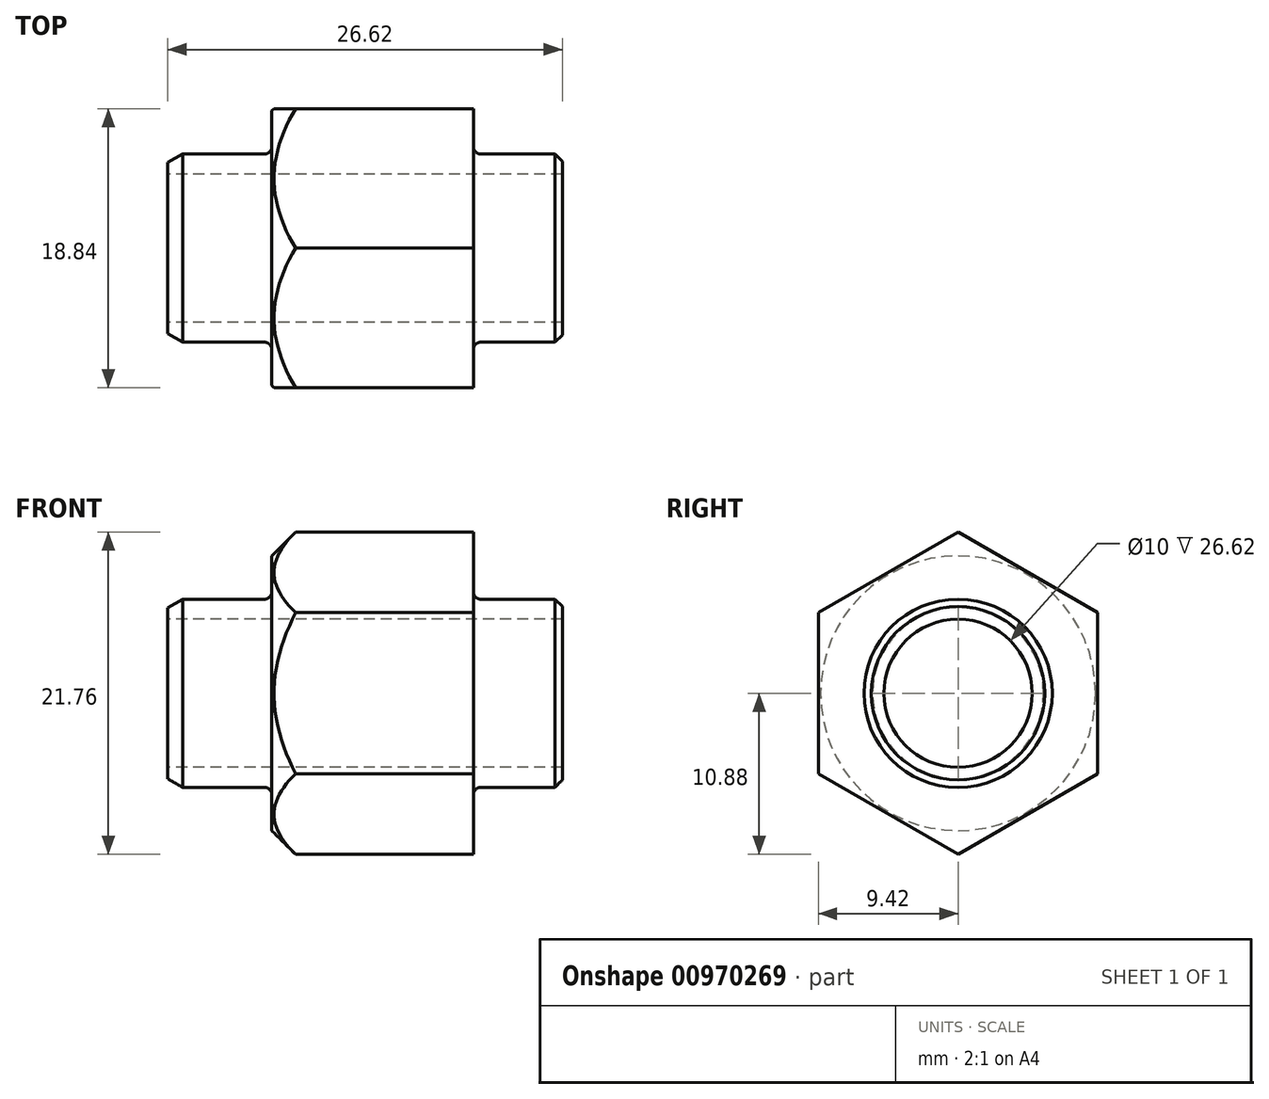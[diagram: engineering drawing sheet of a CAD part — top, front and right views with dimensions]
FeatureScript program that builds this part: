
annotation { "Feature Type Name" : "Feature", "Feature Type Description" : "" }
export const myFeature = defineFeature(function(context is Context, id is Id, definition is map)
    precondition{}
    {
        {
            var Q0;
            Q0=qCreatedBy(makeId("Right.planeOp"),FACE);
            var sketch = newSketch(context, id + "F0", { "sketchPlane" : qUnion([Q0])});
            skCircle(sketch, "E0", {"center": v(0, 0) * mm, "radius": 6.35 * mm});
            skCircle(sketch, "E1.cCircle", {"center": v(0, 0) * mm, "radius": 9.42 * mm, "construction": true});
            skLineSegment(sketch, "E1.0", {"start": v(0, 10.88) * mm, "end": v(9.42, 5.44) * mm});
            skLineSegment(sketch, "E1.1", {"start": v(9.42, 5.44) * mm, "end": v(9.42, -5.44) * mm});
            skLineSegment(sketch, "E1.2", {"start": v(9.42, -5.44) * mm, "end": v(0, -10.88) * mm});
            skLineSegment(sketch, "E1.3", {"start": v(0, -10.88) * mm, "end": v(-9.42, -5.44) * mm});
            skLineSegment(sketch, "E1.4", {"start": v(-9.42, -5.44) * mm, "end": v(-9.42, 5.44) * mm});
            skLineSegment(sketch, "E1.5", {"start": v(-9.42, 5.44) * mm, "end": v(0, 10.88) * mm});
            skPoint(sketch, "E1.0.midPoint", {"position": v(4.7, 8.16) * mm});
            skSolve(sketch);
        }
        {
            var Q0;
            Q0=makeQuery(id+"F0.imprint","IMPRINT",FACE,{"disambiguationData":[TD([[makeQuery(id+"F0.imprint","IMPRINT",EDGE,{"derivedFrom":sQuery(id+"F0.wireOp",EDGE,"E0")}),-1.0]])]});
            var Q1;
            Q1=makeQuery(id+"F0.imprint","IMPRINT",FACE,{"disambiguationData":[TD([[makeQuery(id+"F0.imprint","IMPRINT",EDGE,{"derivedFrom":sQuery(id+"F0.wireOp",EDGE,"E0")}),1.0]])]});
            extrude(context, id + "F1", {"entities" : qUnion([Q0, Q1]), "depth" : 6.8 * mm, "hasSecondDirection" : true, "secondDirectionOppositeDirection" : true, "secondDirectionDepth" : 6.8 * mm});
        }
        {
            var Q0;
            Q0=makeQuery(id+"F0.imprint","IMPRINT",FACE,{"disambiguationData":[TD([[makeQuery(id+"F0.imprint","IMPRINT",EDGE,{"derivedFrom":sQuery(id+"F0.wireOp",EDGE,"E0")}),1.0]])]});
            extrude(context, id + "F2", {"entities" : qUnion([Q0]), "operationType" : NewBodyOperationType.ADD, "oppositeDirection" : true, "depth" : 13.82 * mm, "hasSecondDirection" : true, "secondDirectionOppositeDirection" : false, "secondDirectionDepth" : 12.8 * mm});
        }
        {
            var Q0;
            Q0=qCreatedBy(makeId("Front.planeOp"),FACE);
            var sketch = newSketch(context, id + "F3", { "sketchPlane" : qUnion([Q0])});
            skLineSegment(sketch, "E2.0", {"start": v(-5.2, 10.88) * mm, "end": v(-6.8, 10.88) * mm});
            skLineSegment(sketch, "E2.1", {"start": v(-6.8, 9.28) * mm, "end": v(-6.8, 10.88) * mm});
            skLineSegment(sketch, "E3", {"start": v(-6.8, 9.28) * mm, "end": v(-5.2, 10.88) * mm});
            skPoint(sketch, "E4.orphan", {"position": v(6.8, 10.88) * mm});
            skPoint(sketch, "E5.orphan", {"position": v(-6.8, 5.44) * mm});
            skSolve(sketch);
        }
        {
            var Q0;
            Q0=makeQuery(id+"F3.imprint","IMPRINT",FACE,{"disambiguationData":[TD([[makeQuery(id+"F3.imprint","IMPRINT",EDGE,{"derivedFrom":sQuery(id+"F3.wireOp",EDGE,"E2.0")}),1.0]])]});
            var Q1;
            {var subQ0=sQuery(id+"F0.wireOp",EDGE,"E0");Q1=makeQuery(id+"F2.boolean.opBoolean","SPLIT",FACE,{"disambiguationData":[TD([makeQuery(id+"F2.opExtrude","CAP_FACE",FACE,{"disambiguationData":[OSD([subQ0])],"isStart":true})])],"derivedFrom":makeQuery(id+"F2.opExtrude","SWEPT_FACE",FACE,{"disambiguationData":[OSD([subQ0])]})});}
            revolve(context, id + "F4", {"operationType" : NewBodyOperationType.REMOVE, "entities" : qUnion([Q0]), "axis" : qUnion([Q1]), "revolveType" : RevolveType.FULL, "oppositeDirection" : true});
        }
        {
            var Q0;
            Q0=qCreatedBy(makeId("Right.planeOp"),FACE);
            var sketch = newSketch(context, id + "F5", { "sketchPlane" : qUnion([Q0])});
            skCircle(sketch, "E6", {"center": v(0, 0) * mm, "radius": 5 * mm});
            skSolve(sketch);
        }
        {
            var Q0;
            Q0=makeQuery(id+"F5.imprint","IMPRINT",FACE,{"disambiguationData":[TD([[makeQuery(id+"F5.imprint","IMPRINT",EDGE,{"derivedFrom":sQuery(id+"F5.wireOp",EDGE,"E6")}),1.0]])]});
            extrude(context, id + "F6", {"entities" : qUnion([Q0]), "operationType" : NewBodyOperationType.REMOVE, "endBound" : BoundingType.SYMMETRIC, "depth" : 30 * mm});
        }
        {
            var Q0;
            Q0=makeQuery(id+"F2.opExtrude","CAP_EDGE",EDGE,{"disambiguationData":[OSD([sQuery(id+"F0.wireOp",EDGE,"E0")])],"isStart":false});
            chamfer(context, id + "F7", {"entities" : qUnion([Q0]), "chamferType" : ChamferType.OFFSET_ANGLE, "width" : 1 * mm, "oppositeDirection" : false, "angle" : 30 * degree, "tangentPropagation" : true});
        }
        {
            var Q0;
            Q0=makeQuery(id+"F2.opExtrude","CAP_EDGE",EDGE,{"disambiguationData":[OSD([sQuery(id+"F0.wireOp",EDGE,"E0")])],"isStart":true});
            chamfer(context, id + "F8", {"entities" : qUnion([Q0]), "width" : 0.5 * mm, "tangentPropagation" : true});
        }
        {
            var Q0;
            Q0=makeQuery(id+"F2.boolean.opBoolean","INTERSECT",EDGE,{"derivedFrom":[makeQuery(id+"F1.opExtrude","CAP_FACE",FACE,{"disambiguationData":[OSD([sQuery(id+"F0.wireOp",EDGE,"E1.0"),sQuery(id+"F0.wireOp",EDGE,"E1.1"),sQuery(id+"F0.wireOp",EDGE,"E1.2"),sQuery(id+"F0.wireOp",EDGE,"E1.3"),sQuery(id+"F0.wireOp",EDGE,"E1.4"),sQuery(id+"F0.wireOp",EDGE,"E1.5")])],"isStart":false}),makeQuery(id+"F2.opExtrude","SWEPT_FACE",FACE,{"disambiguationData":[OSD([sQuery(id+"F0.wireOp",EDGE,"E0")])]})]});
            var Q1;
            Q1=makeQuery(id+"F2.boolean.opBoolean","INTERSECT",EDGE,{"derivedFrom":[makeQuery(id+"F1.opExtrude","CAP_FACE",FACE,{"disambiguationData":[OSD([sQuery(id+"F0.wireOp",EDGE,"E1.0"),sQuery(id+"F0.wireOp",EDGE,"E1.1"),sQuery(id+"F0.wireOp",EDGE,"E1.2"),sQuery(id+"F0.wireOp",EDGE,"E1.3"),sQuery(id+"F0.wireOp",EDGE,"E1.4"),sQuery(id+"F0.wireOp",EDGE,"E1.5")])],"isStart":true}),makeQuery(id+"F2.opExtrude","SWEPT_FACE",FACE,{"disambiguationData":[OSD([sQuery(id+"F0.wireOp",EDGE,"E0")])]})]});
            fillet(context, id + "F9", {"entities" : qUnion([Q0, Q1]), "radius" : 0.5 * mm, "tangentPropagation" : true, "conicFillet" : false});
        }
    });
